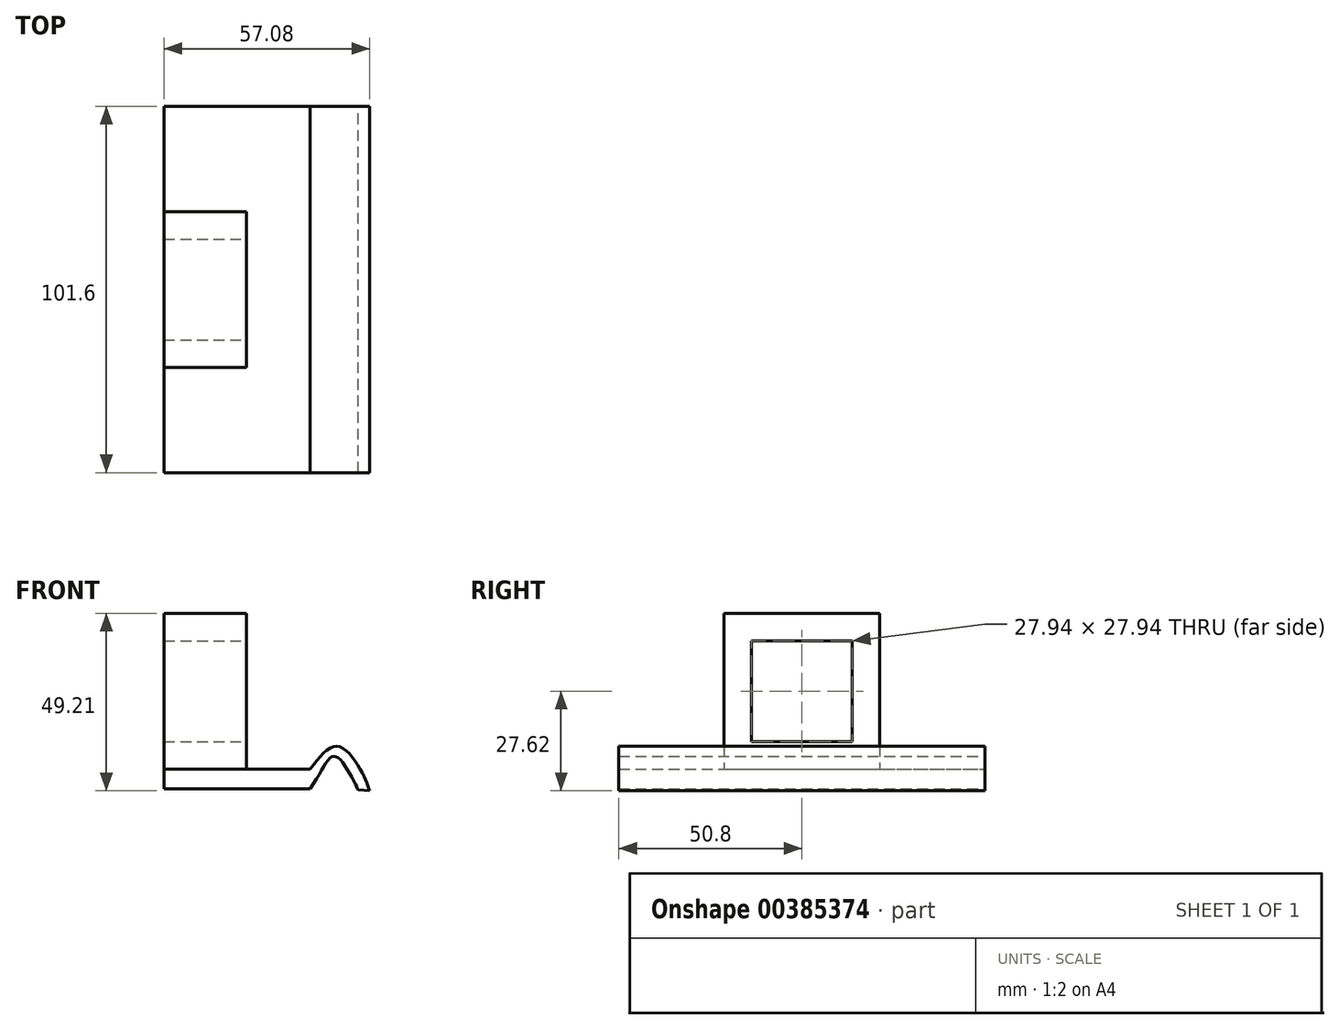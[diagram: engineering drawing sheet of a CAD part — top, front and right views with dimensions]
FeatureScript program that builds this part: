
annotation { "Feature Type Name" : "Feature", "Feature Type Description" : "" }
export const myFeature = defineFeature(function(context is Context, id is Id, definition is map)
    precondition{}
    {
        {
            var Q0;
            Q0=qCreatedBy(makeId("Front.planeOp"),FACE);
            var sketch = newSketch(context, id + "F0", { "sketchPlane" : qUnion([Q0])});
            skLineSegment(sketch, "E0.top", {"start": v(-71.38, 0) * mm, "end": v(-41.44, 0) * mm});
            skLineSegment(sketch, "E1", {"start": v(-71.38, 0) * mm, "end": v(-71.38, -5.47) * mm});
            skLineSegment(sketch, "E2", {"start": v(-71.38, -5.47) * mm, "end": v(-30.8, -5.47) * mm});
            skLineSegment(sketch, "E3", {"start": v(-41.44, 0) * mm, "end": v(-30.8, 0) * mm});
            skFitSpline(sketch, "E4", {"points": [v(-30.8, 0) * mm, v(-23.31, 6.33) * mm, v(-16.98, 0) * mm, v(-14.4, -5.76) * mm, v(-14.1, -6.62) * mm, v(-14.4, -5.47) * mm, v(-14.1, -6.04) * mm], "startDerivative": vector(27.48, 35.88) * mm, "endDerivative": vector(6.13, -14.23) * mm});
            skFitSpline(sketch, "E5", {"points": [v(-30.8, -5.47) * mm, v(-23.31, 3.26) * mm, v(-17.56, -5.76) * mm, v(-17.56, -6.04) * mm], "startDerivative": vector(23.83, 34.82) * mm, "endDerivative": vector(0, -11.58) * mm});
            skLineSegment(sketch, "E6", {"start": v(-17.56, -5.76) * mm, "end": v(-14.1, -6.04) * mm});
            skSolve(sketch);
        }
        {
            var Q0;
            Q0=makeQuery(id+"F0.imprint","IMPRINT",FACE,{"disambiguationData":[TD([[makeQuery(id+"F0.imprint","IMPRINT",EDGE,{"derivedFrom":sQuery(id+"F0.wireOp",EDGE,"E0.top")}),-1.0]])]});
            extrude(context, id + "F1", {"entities" : qUnion([Q0]), "depth" : 101.6 * mm});
        }
        {
            var Q0;
            Q0=qCreatedBy(makeId("Right.planeOp"),FACE);
            cPlane(context, id + "F2", {"entities" : qUnion([Q0]), "cplaneType" : CPlaneType.OFFSET, "offset" : 48.5 * mm, "oppositeDirection" : true, "width" : 152.4 * mm, "height" : 152.4 * mm});
        }
        {
            var Q0;
            Q0=qCreatedBy(id+"F2.planeOp",FACE);
            var sketch = newSketch(context, id + "F3", { "sketchPlane" : qUnion([Q0])});
            skLineSegment(sketch, "E7", {"start": v(-101.6, 21.59) * mm, "end": v(0, 21.59) * mm});
            skLineSegment(sketch, "E8.bottom", {"start": v(-72.4, 43.18) * mm, "end": v(-29.21, 43.18) * mm});
            skLineSegment(sketch, "E8.top", {"start": v(-72.4, 0) * mm, "end": v(-29.21, 0) * mm});
            skLineSegment(sketch, "E8.left", {"start": v(-72.4, 43.18) * mm, "end": v(-72.4, 0) * mm});
            skLineSegment(sketch, "E8.right", {"start": v(-29.21, 43.18) * mm, "end": v(-29.21, 0) * mm});
            skPoint(sketch, "E8.middle", {"position": v(-50.8, 21.59) * mm});
            skLineSegment(sketch, "E9.bottom", {"start": v(-64.77, 35.56) * mm, "end": v(-36.83, 35.56) * mm});
            skLineSegment(sketch, "E9.top", {"start": v(-64.77, 7.62) * mm, "end": v(-36.83, 7.62) * mm});
            skLineSegment(sketch, "E9.left", {"start": v(-64.77, 35.56) * mm, "end": v(-64.77, 7.62) * mm});
            skLineSegment(sketch, "E9.right", {"start": v(-36.83, 35.56) * mm, "end": v(-36.83, 7.62) * mm});
            skSolve(sketch);
        }
        {
            var Q0;
            Q0 = qSketchRegion(id + "F3", true);
            extrude(context, id + "F4", {"entities" : qUnion([Q0]), "operationType" : NewBodyOperationType.ADD, "oppositeDirection" : true, "depth" : 22.86 * mm});
        }
    });
